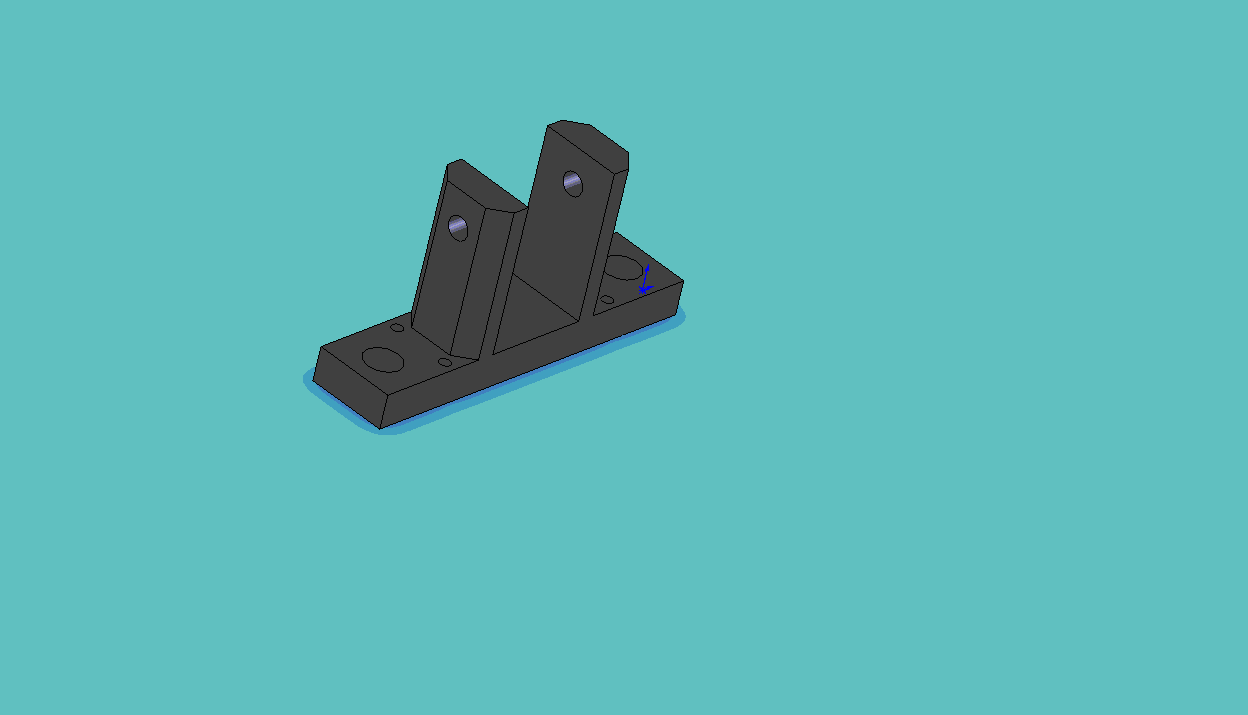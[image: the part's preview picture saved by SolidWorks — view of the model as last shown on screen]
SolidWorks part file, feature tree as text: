
SOLIDWORKS PART (.sldprt)
format: sldprt  version: not decoded by parser v0  size: 114,688 bytes
history: native  units: mm
features: plane x3, sketch x3, cut_extrude x2, material x1, extrude x1, chamfer x1 (+10 scaffold rows collapsed)
feature tree (21):
  scaffold x10  (default folders/planes/origin — collapsed)
  material  "Matériau <non spécifié>"
  plane  "Plan de face"
  plane  "Plan de dessus"
  plane  "Plan de droite"
  sketch  "Esquisse1"  dims[D1=3.0mm D2=16.0mm D3=11.0mm D4=3.0mm D5=31.0mm]
  extrude  "Extrusion1"  Depth=7mm
  sketch  "Esquisse2"  dims[D1=3.2mm D6=1.0mm D2=2.5mm D3=1.0mm D4=1.0mm D5=25.0mm]
  cut_extrude  "Enlèv. mat.-Extru.1"  [1 undecoded]
  sketch  "Esquisse3"  dims[D1=2.0mm D2=3.0mm]
  cut_extrude  "Enlèv. mat.-Extru.2"  [1 undecoded]
  chamfer  "Chanfrein1"  Distance=1.5mm Angle=45deg
decode coverage: 5 of 7 modeling features carry decoded parameters
note: 2 parameter values undecoded
note: suppression state not decoded; provenance and decode notes live in map.json
